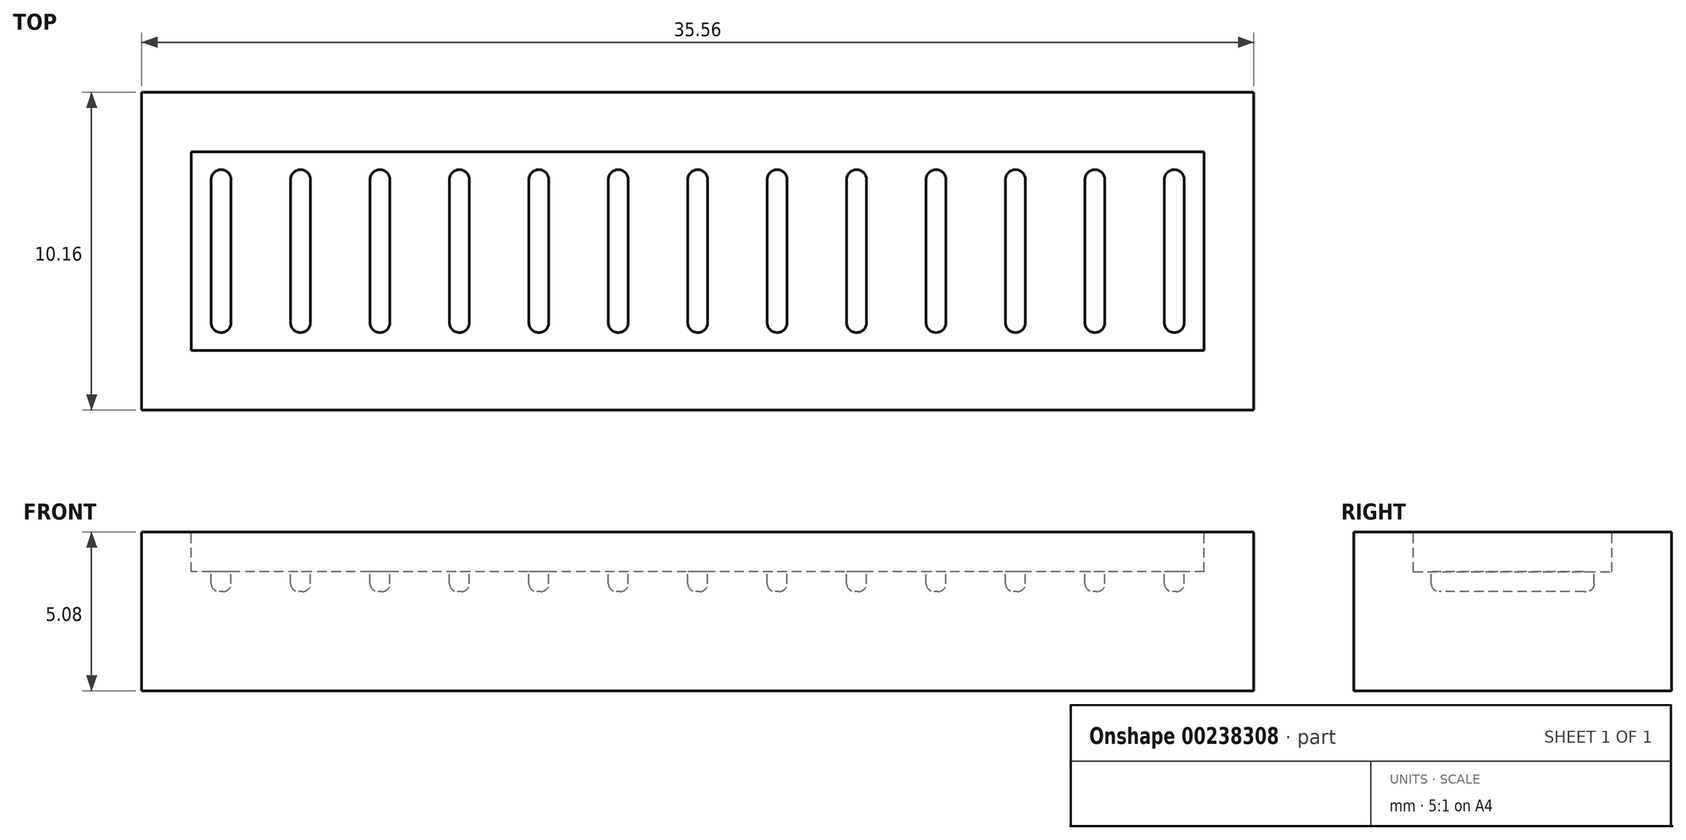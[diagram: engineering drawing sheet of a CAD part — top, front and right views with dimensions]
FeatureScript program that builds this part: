
annotation { "Feature Type Name" : "Feature", "Feature Type Description" : "" }
export const myFeature = defineFeature(function(context is Context, id is Id, definition is map)
    precondition{}
    {
        {
            var Q0;
            Q0=qCreatedBy(makeId("Top.planeOp"),FACE);
            var sketch = newSketch(context, id + "F0", { "sketchPlane" : qUnion([Q0])});
            skLineSegment(sketch, "E0.bottom", {"start": v(17.78, -5.08) * mm, "end": v(-17.78, -5.08) * mm});
            skLineSegment(sketch, "E0.top", {"start": v(17.78, 5.08) * mm, "end": v(-17.78, 5.08) * mm});
            skLineSegment(sketch, "E0.left", {"start": v(17.78, -5.08) * mm, "end": v(17.78, 5.08) * mm});
            skLineSegment(sketch, "E0.right", {"start": v(-17.78, -5.08) * mm, "end": v(-17.78, 5.08) * mm});
            skPoint(sketch, "E0.middle", {"position": v(0, 0) * mm});
            skSolve(sketch);
        }
        {
            var Q0;
            Q0=makeQuery(id+"F0.imprint","IMPRINT",FACE,{"disambiguationData":[TD([[makeQuery(id+"F0.imprint","IMPRINT",EDGE,{"derivedFrom":sQuery(id+"F0.wireOp",EDGE,"E0.bottom")}),-1.0]])]});
            extrude(context, id + "F1", {"entities" : qUnion([Q0]), "depth" : 5.08 * mm});
        }
        {
            var Q0;
            Q0=makeQuery(id+"F1.opExtrude","CAP_FACE",FACE,{"disambiguationData":[OSD([sQuery(id+"F0.wireOp",EDGE,"E0.bottom"),sQuery(id+"F0.wireOp",EDGE,"E0.top"),sQuery(id+"F0.wireOp",EDGE,"E0.left"),sQuery(id+"F0.wireOp",EDGE,"E0.right")])],"isStart":false});
            var sketch = newSketch(context, id + "F2", { "sketchPlane" : qUnion([Q0])});
            skLineSegment(sketch, "E1.bottom", {"start": v(16.2, -3.18) * mm, "end": v(-16.2, -3.18) * mm});
            skLineSegment(sketch, "E1.top", {"start": v(16.2, 3.18) * mm, "end": v(-16.2, 3.18) * mm});
            skLineSegment(sketch, "E1.left", {"start": v(16.2, -3.18) * mm, "end": v(16.2, 3.17) * mm});
            skLineSegment(sketch, "E1.right", {"start": v(-16.2, -3.18) * mm, "end": v(-16.2, 3.17) * mm});
            skPoint(sketch, "E1.middle", {"position": v(0, 0) * mm});
            skSolve(sketch);
        }
        {
            var Q0;
            Q0=qSketchRegion(id+"F2",true);
            extrude(context, id + "F3", {"entities" : qUnion([Q0]), "operationType" : NewBodyOperationType.REMOVE, "oppositeDirection" : true, "depth" : 1.27 * mm});
        }
        {
            var Q0;
            Q0=makeQuery(id+"F3.boolean.opBoolean","COPY",FACE,{"derivedFrom":makeQuery(id+"F3.opExtrude","CAP_FACE",FACE,{"disambiguationData":[OSD([sQuery(id+"F2.wireOp",EDGE,"E1.bottom"),sQuery(id+"F2.wireOp",EDGE,"E1.top"),sQuery(id+"F2.wireOp",EDGE,"E1.left"),sQuery(id+"F2.wireOp",EDGE,"E1.right")])],"isStart":false})});
            var sketch = newSketch(context, id + "F4", { "sketchPlane" : qUnion([Q0])});
            skLineSegment(sketch, "E2", {"start": v(0, 2.29) * mm, "end": v(0, -2.29) * mm});
            skArc(sketch, "E3.0.startCap", {"start": v(-0.32, 2.29) * mm, "mid": v(0, 2.6) * mm, "end": v(0.32, 2.29) * mm});
            skArc(sketch, "E3.0.endCap", {"start": v(0.32, -2.29) * mm, "mid": v(0, -2.6) * mm, "end": v(-0.32, -2.29) * mm});
            skLineSegment(sketch, "E3.0.left", {"start": v(0.32, 2.29) * mm, "end": v(0.32, -2.29) * mm});
            skLineSegment(sketch, "E3.0.right", {"start": v(-0.32, 2.29) * mm, "end": v(-0.32, -2.29) * mm});
            skArc(sketch, "E4.1.0.0", {"start": v(2.22, 2.29) * mm, "mid": v(2.54, 2.6) * mm, "end": v(2.86, 2.29) * mm});
            skArc(sketch, "E4.1.0.1", {"start": v(2.86, -2.29) * mm, "mid": v(2.54, -2.6) * mm, "end": v(2.22, -2.29) * mm});
            skLineSegment(sketch, "E4.1.0.2", {"start": v(2.86, 2.29) * mm, "end": v(2.86, -2.29) * mm});
            skLineSegment(sketch, "E4.1.0.3", {"start": v(2.22, 2.29) * mm, "end": v(2.22, -2.29) * mm});
            skLineSegment(sketch, "E4.1.0.4", {"start": v(2.54, 2.29) * mm, "end": v(2.54, -2.29) * mm});
            skArc(sketch, "E4.2.0.0", {"start": v(4.76, 2.29) * mm, "mid": v(5.08, 2.6) * mm, "end": v(5.4, 2.29) * mm});
            skArc(sketch, "E4.2.0.1", {"start": v(5.4, -2.29) * mm, "mid": v(5.08, -2.6) * mm, "end": v(4.76, -2.29) * mm});
            skLineSegment(sketch, "E4.2.0.2", {"start": v(5.4, 2.29) * mm, "end": v(5.4, -2.29) * mm});
            skLineSegment(sketch, "E4.2.0.3", {"start": v(4.76, 2.29) * mm, "end": v(4.76, -2.29) * mm});
            skLineSegment(sketch, "E4.2.0.4", {"start": v(5.08, 2.29) * mm, "end": v(5.08, -2.29) * mm});
            skArc(sketch, "E4.3.0.0", {"start": v(7.3, 2.29) * mm, "mid": v(7.62, 2.6) * mm, "end": v(7.94, 2.29) * mm});
            skArc(sketch, "E4.3.0.1", {"start": v(7.94, -2.29) * mm, "mid": v(7.62, -2.6) * mm, "end": v(7.3, -2.29) * mm});
            skLineSegment(sketch, "E4.3.0.2", {"start": v(7.94, 2.29) * mm, "end": v(7.94, -2.29) * mm});
            skLineSegment(sketch, "E4.3.0.3", {"start": v(7.3, 2.29) * mm, "end": v(7.3, -2.29) * mm});
            skLineSegment(sketch, "E4.3.0.4", {"start": v(7.62, 2.29) * mm, "end": v(7.62, -2.29) * mm});
            skArc(sketch, "E4.4.0.0", {"start": v(9.84, 2.29) * mm, "mid": v(10.16, 2.6) * mm, "end": v(10.48, 2.29) * mm});
            skArc(sketch, "E4.4.0.1", {"start": v(10.48, -2.29) * mm, "mid": v(10.16, -2.6) * mm, "end": v(9.84, -2.29) * mm});
            skLineSegment(sketch, "E4.4.0.2", {"start": v(10.48, 2.29) * mm, "end": v(10.48, -2.29) * mm});
            skLineSegment(sketch, "E4.4.0.3", {"start": v(9.84, 2.29) * mm, "end": v(9.84, -2.29) * mm});
            skLineSegment(sketch, "E4.4.0.4", {"start": v(10.16, 2.29) * mm, "end": v(10.16, -2.29) * mm});
            skLineSegment(sketch, "E4.direction1", {"start": v(-0.32, -2.29) * mm, "end": v(2.22, -2.29) * mm, "construction": true});
            skLineSegment(sketch, "E5.1.0.0", {"start": v(-2.86, 2.29) * mm, "end": v(-2.86, -2.29) * mm});
            skLineSegment(sketch, "E5.1.0.1", {"start": v(-2.22, 2.29) * mm, "end": v(-2.22, -2.29) * mm});
            skArc(sketch, "E5.1.0.2", {"start": v(-2.22, -2.29) * mm, "mid": v(-2.54, -2.6) * mm, "end": v(-2.86, -2.29) * mm});
            skArc(sketch, "E5.1.0.3", {"start": v(-2.86, 2.29) * mm, "mid": v(-2.54, 2.6) * mm, "end": v(-2.22, 2.29) * mm});
            skLineSegment(sketch, "E5.1.0.4", {"start": v(-2.54, 2.29) * mm, "end": v(-2.54, -2.29) * mm});
            skLineSegment(sketch, "E5.2.0.0", {"start": v(-5.4, 2.29) * mm, "end": v(-5.4, -2.29) * mm});
            skLineSegment(sketch, "E5.2.0.1", {"start": v(-4.76, 2.29) * mm, "end": v(-4.76, -2.29) * mm});
            skArc(sketch, "E5.2.0.2", {"start": v(-4.76, -2.29) * mm, "mid": v(-5.08, -2.6) * mm, "end": v(-5.4, -2.29) * mm});
            skArc(sketch, "E5.2.0.3", {"start": v(-5.4, 2.29) * mm, "mid": v(-5.08, 2.6) * mm, "end": v(-4.76, 2.29) * mm});
            skLineSegment(sketch, "E5.2.0.4", {"start": v(-5.08, 2.29) * mm, "end": v(-5.08, -2.29) * mm});
            skLineSegment(sketch, "E5.3.0.0", {"start": v(-7.94, 2.29) * mm, "end": v(-7.94, -2.29) * mm});
            skLineSegment(sketch, "E5.3.0.1", {"start": v(-7.3, 2.29) * mm, "end": v(-7.3, -2.29) * mm});
            skArc(sketch, "E5.3.0.2", {"start": v(-7.3, -2.29) * mm, "mid": v(-7.62, -2.6) * mm, "end": v(-7.94, -2.29) * mm});
            skArc(sketch, "E5.3.0.3", {"start": v(-7.94, 2.29) * mm, "mid": v(-7.62, 2.6) * mm, "end": v(-7.3, 2.29) * mm});
            skLineSegment(sketch, "E5.3.0.4", {"start": v(-7.62, 2.29) * mm, "end": v(-7.62, -2.29) * mm});
            skLineSegment(sketch, "E5.4.0.0", {"start": v(-10.48, 2.29) * mm, "end": v(-10.48, -2.29) * mm});
            skLineSegment(sketch, "E5.4.0.1", {"start": v(-9.84, 2.29) * mm, "end": v(-9.84, -2.29) * mm});
            skArc(sketch, "E5.4.0.2", {"start": v(-9.84, -2.29) * mm, "mid": v(-10.16, -2.6) * mm, "end": v(-10.48, -2.29) * mm});
            skArc(sketch, "E5.4.0.3", {"start": v(-10.48, 2.29) * mm, "mid": v(-10.16, 2.6) * mm, "end": v(-9.84, 2.29) * mm});
            skLineSegment(sketch, "E5.4.0.4", {"start": v(-10.16, 2.29) * mm, "end": v(-10.16, -2.29) * mm});
            skLineSegment(sketch, "E5.direction1", {"start": v(-0.32, -2.29) * mm, "end": v(-2.86, -2.29) * mm, "construction": true});
            skArc(sketch, "E6.0.5.0", {"start": v(12.38, 2.29) * mm, "mid": v(12.7, 2.6) * mm, "end": v(13.02, 2.29) * mm});
            skArc(sketch, "E6.4.5.0", {"start": v(13.02, -2.29) * mm, "mid": v(12.7, -2.6) * mm, "end": v(12.38, -2.29) * mm});
            skLineSegment(sketch, "E6.8.5.0", {"start": v(13.02, 2.29) * mm, "end": v(13.02, -2.29) * mm});
            skLineSegment(sketch, "E6.11.5.0", {"start": v(12.38, 2.29) * mm, "end": v(12.38, -2.29) * mm});
            skLineSegment(sketch, "E6.14.5.0", {"start": v(12.7, 2.29) * mm, "end": v(12.7, -2.29) * mm});
            skArc(sketch, "E6.0.6.0", {"start": v(14.92, 2.29) * mm, "mid": v(15.24, 2.6) * mm, "end": v(15.56, 2.29) * mm});
            skArc(sketch, "E6.4.6.0", {"start": v(15.56, -2.29) * mm, "mid": v(15.24, -2.6) * mm, "end": v(14.92, -2.29) * mm});
            skLineSegment(sketch, "E6.8.6.0", {"start": v(15.56, 2.29) * mm, "end": v(15.56, -2.29) * mm});
            skLineSegment(sketch, "E6.11.6.0", {"start": v(14.92, 2.29) * mm, "end": v(14.92, -2.29) * mm});
            skLineSegment(sketch, "E6.14.6.0", {"start": v(15.24, 2.29) * mm, "end": v(15.24, -2.29) * mm});
            skLineSegment(sketch, "E7.0.5.0", {"start": v(-13.02, 2.29) * mm, "end": v(-13.02, -2.29) * mm});
            skLineSegment(sketch, "E7.3.5.0", {"start": v(-12.38, 2.29) * mm, "end": v(-12.38, -2.29) * mm});
            skArc(sketch, "E7.6.5.0", {"start": v(-12.38, -2.29) * mm, "mid": v(-12.7, -2.6) * mm, "end": v(-13.02, -2.29) * mm});
            skArc(sketch, "E7.10.5.0", {"start": v(-13.02, 2.29) * mm, "mid": v(-12.7, 2.6) * mm, "end": v(-12.38, 2.29) * mm});
            skLineSegment(sketch, "E7.14.5.0", {"start": v(-12.7, 2.29) * mm, "end": v(-12.7, -2.29) * mm});
            skLineSegment(sketch, "E7.0.6.0", {"start": v(-15.56, 2.29) * mm, "end": v(-15.56, -2.29) * mm});
            skLineSegment(sketch, "E7.3.6.0", {"start": v(-14.92, 2.29) * mm, "end": v(-14.92, -2.29) * mm});
            skArc(sketch, "E7.6.6.0", {"start": v(-14.92, -2.29) * mm, "mid": v(-15.24, -2.6) * mm, "end": v(-15.56, -2.29) * mm});
            skArc(sketch, "E7.10.6.0", {"start": v(-15.56, 2.29) * mm, "mid": v(-15.24, 2.6) * mm, "end": v(-14.92, 2.29) * mm});
            skLineSegment(sketch, "E7.14.6.0", {"start": v(-15.24, 2.29) * mm, "end": v(-15.24, -2.29) * mm});
            skSolve(sketch);
        }
        {
            var Q0;
            Q0=qSketchRegion(id+"F4",true);
            extrude(context, id + "F5", {"entities" : qUnion([Q0]), "operationType" : NewBodyOperationType.REMOVE, "oppositeDirection" : true, "depth" : 0.64 * mm});
        }
        {
            var Q0;
            Q0=makeQuery(id+"F5.boolean.opBoolean","COPY",EDGE,{"derivedFrom":makeQuery(id+"F5.opExtrude","CAP_EDGE",EDGE,{"disambiguationData":[OSD([sQuery(id+"F4.wireOp",EDGE,"E5.4.0.0")])],"isStart":false})});
            var Q1;
            Q1=makeQuery(id+"F5.boolean.opBoolean","COPY",EDGE,{"derivedFrom":makeQuery(id+"F5.opExtrude","CAP_EDGE",EDGE,{"disambiguationData":[OSD([sQuery(id+"F4.wireOp",EDGE,"E5.3.0.0")])],"isStart":false})});
            var Q2;
            Q2=makeQuery(id+"F5.boolean.opBoolean","COPY",EDGE,{"derivedFrom":makeQuery(id+"F5.opExtrude","CAP_EDGE",EDGE,{"disambiguationData":[OSD([sQuery(id+"F4.wireOp",EDGE,"E5.2.0.0")])],"isStart":false})});
            var Q3;
            Q3=makeQuery(id+"F5.boolean.opBoolean","COPY",EDGE,{"derivedFrom":makeQuery(id+"F5.opExtrude","CAP_EDGE",EDGE,{"disambiguationData":[OSD([sQuery(id+"F4.wireOp",EDGE,"E5.1.0.0")])],"isStart":false})});
            var Q4;
            Q4=makeQuery(id+"F5.boolean.opBoolean","COPY",EDGE,{"derivedFrom":makeQuery(id+"F5.opExtrude","CAP_EDGE",EDGE,{"disambiguationData":[OSD([sQuery(id+"F4.wireOp",EDGE,"E3.0.right")])],"isStart":false})});
            var Q5;
            Q5=makeQuery(id+"F5.boolean.opBoolean","COPY",EDGE,{"derivedFrom":makeQuery(id+"F5.opExtrude","CAP_EDGE",EDGE,{"disambiguationData":[OSD([sQuery(id+"F4.wireOp",EDGE,"E4.1.0.3")])],"isStart":false})});
            var Q6;
            Q6=makeQuery(id+"F5.boolean.opBoolean","COPY",EDGE,{"derivedFrom":makeQuery(id+"F5.opExtrude","CAP_EDGE",EDGE,{"disambiguationData":[OSD([sQuery(id+"F4.wireOp",EDGE,"E4.2.0.3")])],"isStart":false})});
            var Q7;
            Q7=makeQuery(id+"F5.boolean.opBoolean","COPY",EDGE,{"derivedFrom":makeQuery(id+"F5.opExtrude","CAP_EDGE",EDGE,{"disambiguationData":[OSD([sQuery(id+"F4.wireOp",EDGE,"E4.3.0.3")])],"isStart":false})});
            var Q8;
            Q8=makeQuery(id+"F5.boolean.opBoolean","COPY",EDGE,{"derivedFrom":makeQuery(id+"F5.opExtrude","CAP_EDGE",EDGE,{"disambiguationData":[OSD([sQuery(id+"F4.wireOp",EDGE,"E4.4.0.3")])],"isStart":false})});
            var Q9;
            Q9=makeQuery(id+"F5.boolean.opBoolean","COPY",EDGE,{"derivedFrom":makeQuery(id+"F5.opExtrude","CAP_EDGE",EDGE,{"disambiguationData":[OSD([sQuery(id+"F4.wireOp",EDGE,"E7.0.6.0")])],"isStart":false})});
            var Q10;
            Q10=makeQuery(id+"F5.boolean.opBoolean","COPY",EDGE,{"derivedFrom":makeQuery(id+"F5.opExtrude","CAP_EDGE",EDGE,{"disambiguationData":[OSD([sQuery(id+"F4.wireOp",EDGE,"E7.0.5.0")])],"isStart":false})});
            var Q11;
            Q11=makeQuery(id+"F5.boolean.opBoolean","COPY",EDGE,{"derivedFrom":makeQuery(id+"F5.opExtrude","CAP_EDGE",EDGE,{"disambiguationData":[OSD([sQuery(id+"F4.wireOp",EDGE,"E6.11.5.0")])],"isStart":false})});
            var Q12;
            Q12=makeQuery(id+"F5.boolean.opBoolean","COPY",EDGE,{"derivedFrom":makeQuery(id+"F5.opExtrude","CAP_EDGE",EDGE,{"disambiguationData":[OSD([sQuery(id+"F4.wireOp",EDGE,"E6.11.6.0")])],"isStart":false})});
            fillet(context, id + "F6", {"entities" : qUnion([Q0, Q1, Q2, Q3, Q4, Q5, Q6, Q7, Q8, Q9, Q10, Q11, Q12]), "radius" : 0.25 * mm, "tangentPropagation" : true, "allowEdgeOverflow" : false});
        }
    });
